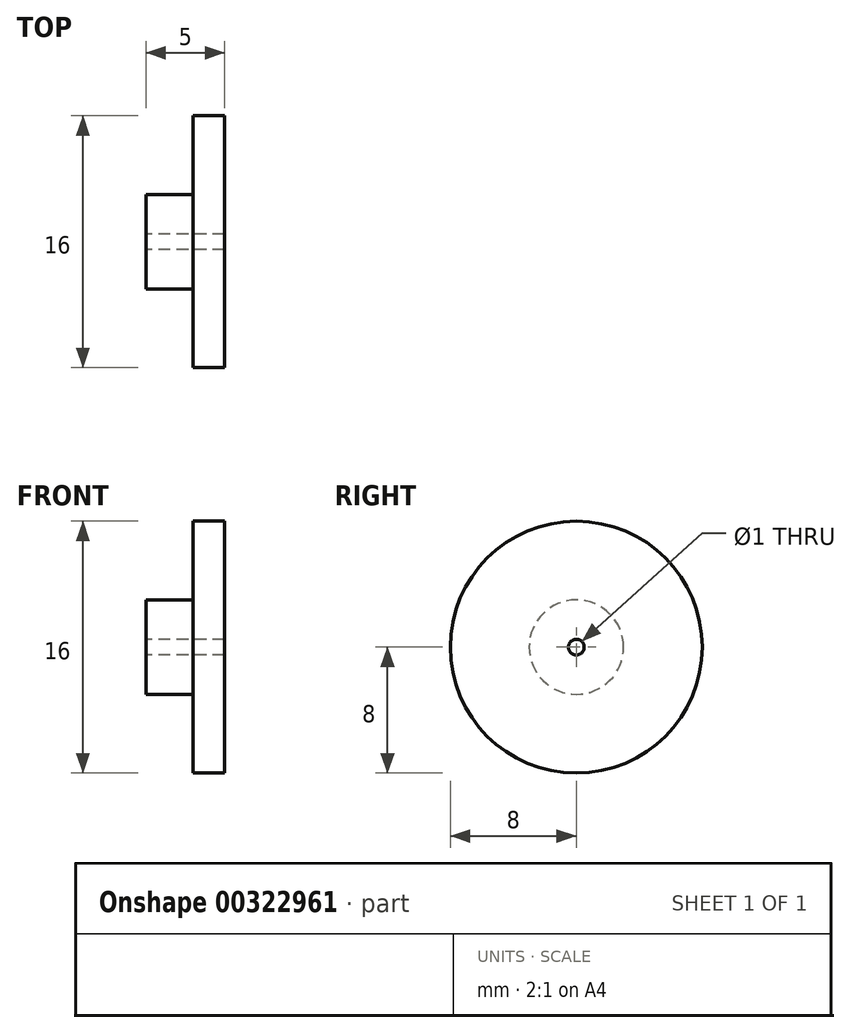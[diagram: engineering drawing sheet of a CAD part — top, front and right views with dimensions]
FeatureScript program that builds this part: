
annotation { "Feature Type Name" : "Feature", "Feature Type Description" : "" }
export const myFeature = defineFeature(function(context is Context, id is Id, definition is map)
    precondition{}
    {
        {
            var Q0;
            Q0=qCreatedBy(makeId("Front.planeOp"),FACE);
            var sketch = newSketch(context, id + "F0", { "sketchPlane" : qUnion([Q0])});
            skLineSegment(sketch, "E0", {"start": v(0, 0) * mm, "end": v(0, 0.5) * mm, "construction": true});
            skLineSegment(sketch, "E1", {"start": v(0, 0.5) * mm, "end": v(5, 0.5) * mm});
            skLineSegment(sketch, "E2", {"start": v(5, 0.5) * mm, "end": v(5, 8) * mm});
            skLineSegment(sketch, "E3", {"start": v(5, 8) * mm, "end": v(3, 8) * mm});
            skLineSegment(sketch, "E4", {"start": v(3, 8) * mm, "end": v(3, 0.5) * mm, "construction": true});
            skLineSegment(sketch, "E5", {"start": v(3, 0.5) * mm, "end": v(3, 3) * mm, "construction": true});
            skLineSegment(sketch, "E6", {"start": v(3, 3) * mm, "end": v(0, 3) * mm});
            skLineSegment(sketch, "E7", {"start": v(0, 3) * mm, "end": v(0, 0.5) * mm});
            skLineSegment(sketch, "E8", {"start": v(3, 3) * mm, "end": v(3, 8) * mm});
            skLineSegment(sketch, "E9", {"start": v(0.11, 0) * mm, "end": v(7.7, 0) * mm, "construction": true});
            skSolve(sketch);
        }
        {
            var Q0;
            Q0 = qSketchRegion(id + "F0", true);
            var Q1;
            Q1=sQuery(id+"F0.wireOp",EDGE,"E9");
            revolve(context, id + "F1", {"entities" : qUnion([Q0]), "axis" : qUnion([Q1]), "revolveType" : RevolveType.FULL});
        }
    });
